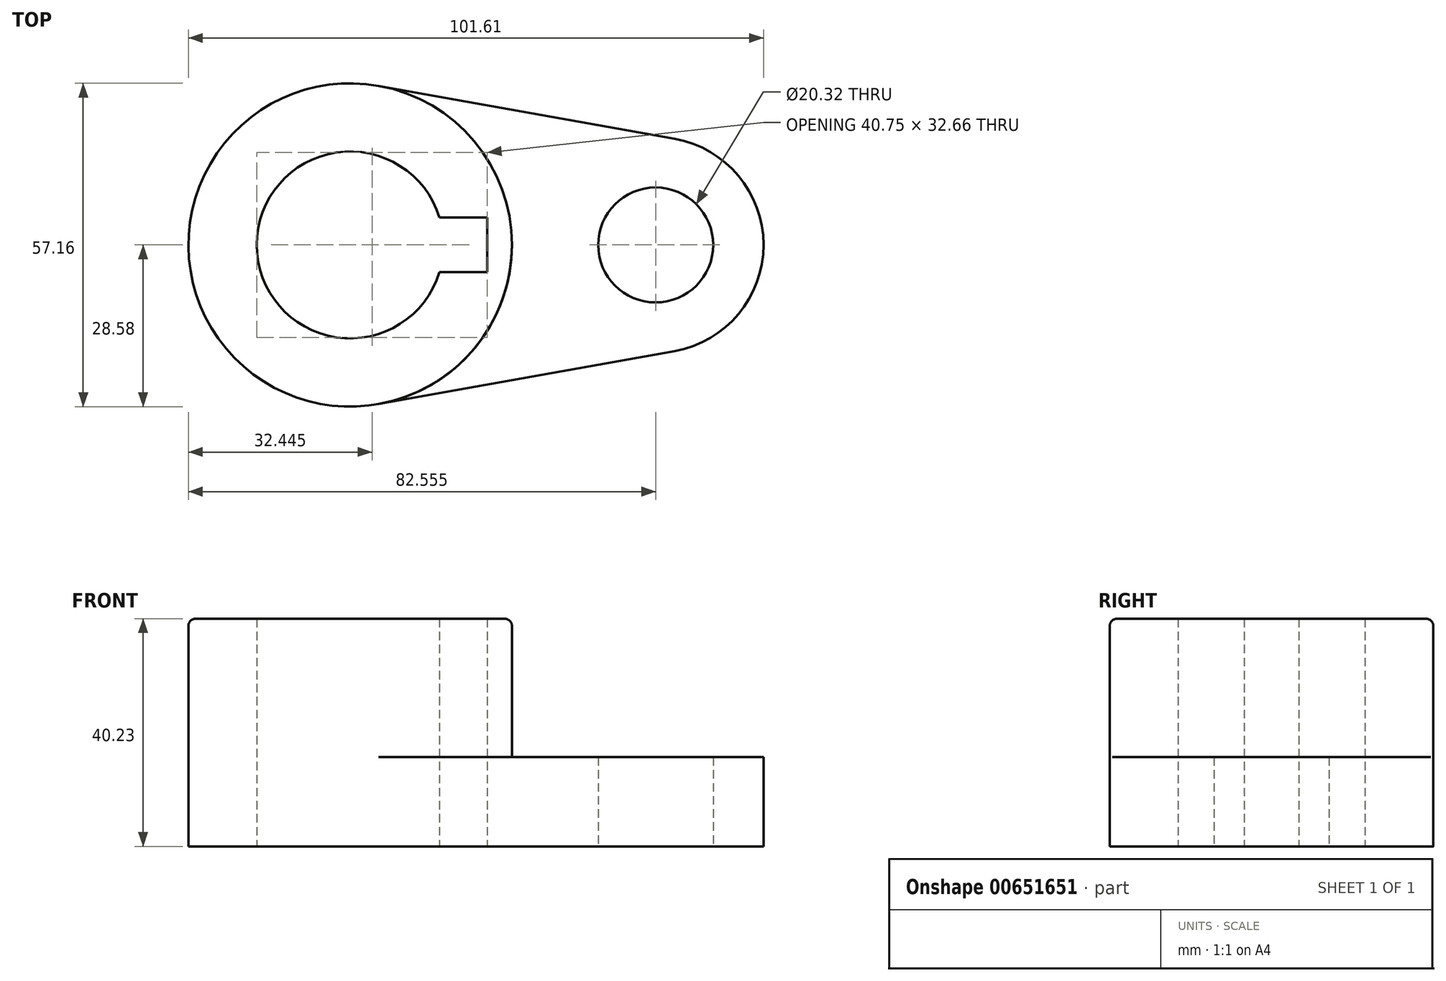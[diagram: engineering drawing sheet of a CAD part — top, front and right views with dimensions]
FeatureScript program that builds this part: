
annotation { "Feature Type Name" : "Feature", "Feature Type Description" : "" }
export const myFeature = defineFeature(function(context is Context, id is Id, definition is map)
    precondition{}
    {
        {
            var Q0;
            Q0=qCreatedBy(makeId("Top.planeOp"),FACE);
            var sketch = newSketch(context, id + "F0", { "sketchPlane" : qUnion([Q0])});
            skCircle(sketch, "E0", {"center": v(0, 0) * mm, "radius": 28.58 * mm});
            skCircle(sketch, "E1", {"center": v(53.98, 0) * mm, "radius": 19.05 * mm});
            skLineSegment(sketch, "E2", {"start": v(5.04, 28.13) * mm, "end": v(57.34, 18.75) * mm});
            skLineSegment(sketch, "E3", {"start": v(5.04, -28.13) * mm, "end": v(57.34, -18.75) * mm});
            skArc(sketch, "E4", {"start": v(15.79, 4.83) * mm, "mid": v(-16.51, 0) * mm, "end": v(15.79, -4.83) * mm});
            skCircle(sketch, "E5", {"center": v(53.98, 0) * mm, "radius": 10.16 * mm});
            skLineSegment(sketch, "E6", {"start": v(15.79, 4.83) * mm, "end": v(24.24, 4.83) * mm});
            skLineSegment(sketch, "E7", {"start": v(24.24, 4.83) * mm, "end": v(24.24, -4.83) * mm});
            skLineSegment(sketch, "E8", {"start": v(24.24, -4.83) * mm, "end": v(15.79, -4.83) * mm});
            skSolve(sketch);
        }
        {
            var Q0;
            Q0=makeQuery(id+"F0.imprint","IMPRINT",FACE,{"disambiguationData":[TD([[makeQuery(id+"F0.imprint","IMPRINT",EDGE,{"derivedFrom":sQuery(id+"F0.wireOp",EDGE,"E4")}),-1.0]])]});
            extrude(context, id + "F1", {"entities" : qUnion([Q0]), "depth" : 40.23 * mm, "offsetDistance" : 25.4 * mm});
        }
        {
            var Q0;
            Q0=makeQuery(id+"F0.imprint","IMPRINT",FACE,{"disambiguationData":[TD([[makeQuery(id+"F0.imprint","IMPRINT",EDGE,{"derivedFrom":sQuery(id+"F0.wireOp",EDGE,"E5")}),-1.0]])]});
            var Q1;
            {var subQ0=sQuery(id+"F0.wireOp",EDGE,"E2");Q1=makeQuery(id+"F0.imprint","IMPRINT",FACE,{"disambiguationData":[TD([[makeQuery(id+"F0.imprint","IMPRINT",EDGE,{"derivedFrom":subQ0}),-1.0]])]});}
            extrude(context, id + "F2", {"entities" : qUnion([Q0, Q1]), "operationType" : NewBodyOperationType.ADD, "depth" : 15.77 * mm, "offsetDistance" : 25.4 * mm});
        }
        {
            var Q0;
            Q0=makeQuery(id+"F1.opExtrude","CAP_EDGE",EDGE,{"disambiguationData":[OSD([sQuery(id+"F0.wireOp",EDGE,"E0")])],"isStart":false});
            fillet(context, id + "F3", {"entities" : qUnion([Q0]), "radius" : 1.27 * mm, "tangentPropagation" : true, "allowEdgeOverflow" : false});
        }
    });
